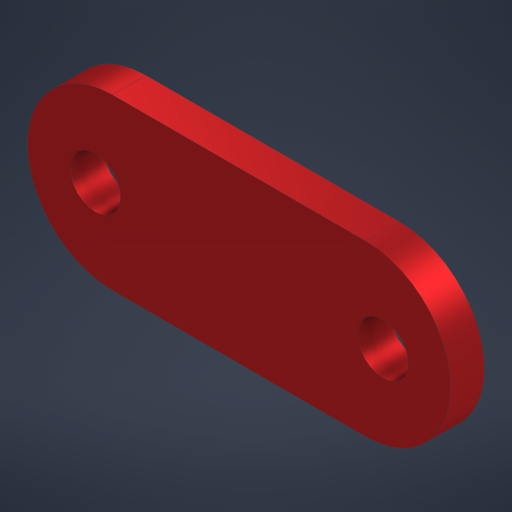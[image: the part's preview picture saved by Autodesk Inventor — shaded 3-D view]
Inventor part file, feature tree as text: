
AUTODESK INVENTOR PART (.ipt)
format: ipt  version: 2023 (Build 270158000, 158)  size: 191,488 bytes
history: native  units: mm
features: extrude x2, sketch x2, fillet x1
ambient origin geometry x8: Origin, YZ Plane, XZ Plane, XY Plane, X Axis, Y Axis, Z Axis, Center Point
bodies: Solid1 (feature_tree)
feature tree (5):
  extrude  "Extrusion1"  Depth=10.0mm
  fillet  "Fillet1"  Radius=2.0mm
  extrude  "Extrusion3"  Depth=10.0mm
  sketch  "Sketch1"  dims[d0=25.0mm d1=10.0mm d2=2.0mm d3=0.0mm]
  sketch  "Sketch2"  dims[d4=5.0mm d9=1.0mm d10=17.0mm d11=3.0mm d12=3.0mm d13=10.0mm d14=0.0mm]
